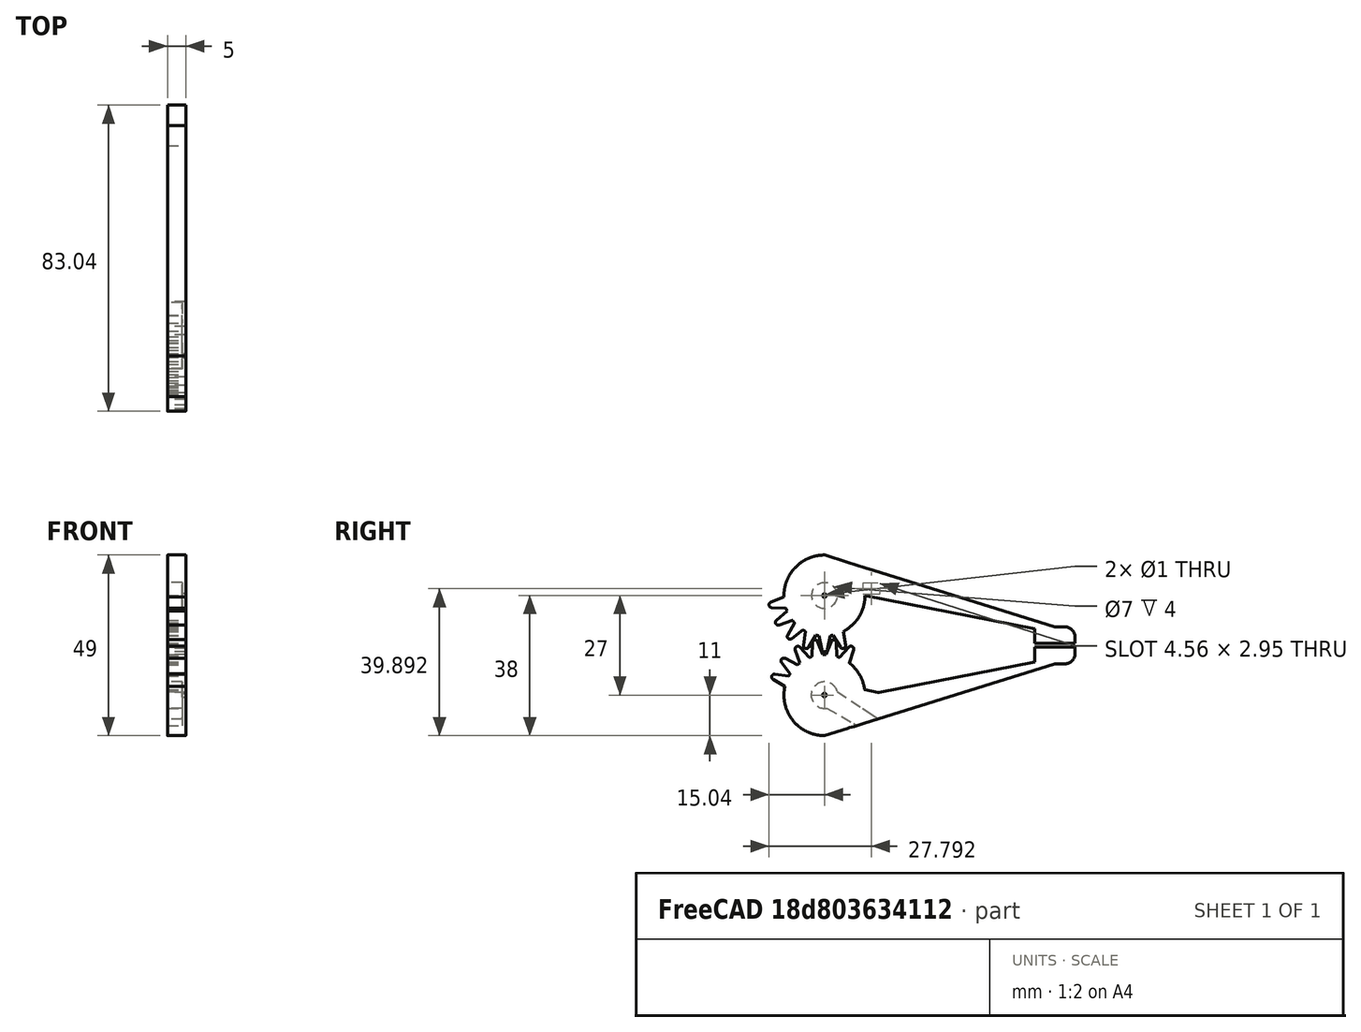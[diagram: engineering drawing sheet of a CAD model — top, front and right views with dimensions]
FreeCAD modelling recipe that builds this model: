
FCSTD DOCUMENT  (FreeCAD 0.20R29177 +426 (Git))
Label: gripper
License: All rights reserved
LicenseURL: http://en.wikipedia.org/wiki/All_rights_reserved
objects: Sketcher::SketchObject×10, PartDesign::Pocket×6, PartDesign::Pad×4, Mesh::Feature×2, PartDesign::PolarPattern×2, PartDesign::Body×2
note: 34 computed .brp shape members not serialized (recipe doc carries the construction recipe); baked Part::Feature solids carry a one-line shape summary decoded from their .brp

FEATURE [Mesh::Feature] ServoGripper90g_v1_A  label="ServoGripper90g_v1-A"
  Placement = pos=(0,0,-27) rot=(0,0,1;0rad)
FEATURE [Sketcher::SketchObject] Sketch  label="larm"
  FullyConstrained = true
  MapMode = 5
  Placement = pos=(0,0,0) rot=(0.57735,0.57735,0.57735;2.0944rad)
  Support = -> [YZ_Plane]
  sketch-geometry (9):
    g0: ArcOfCircle CenterX=0 CenterY=0 CenterZ=0 NormalX=0 NormalY=0 NormalZ=1 AngleXU=0 Radius=11 StartAngle=0 EndAngle=5.0362
    g1: LineSegment StartX=57 StartY=13 StartZ=0 EndX=68 EndY=13 EndZ=0
    g2: LineSegment StartX=68 StartY=13 StartZ=0 EndX=68 EndY=11.2 EndZ=0
    g3: LineSegment StartX=65.3 StartY=8.5 StartZ=0 EndX=62.5 EndY=8.5 EndZ=0
    g4: LineSegment StartX=57 StartY=9 StartZ=0 EndX=57 EndY=13 EndZ=0
    g5: GeomPoint X=62.5 Y=8.5 Z=0
    g6: LineSegment StartX=11 StartY=0 StartZ=0 EndX=57 EndY=9 EndZ=0
    g7: LineSegment StartX=62.5 StartY=8.5 StartZ=0 EndX=3.5 EndY=-10.4283 EndZ=0
    g8: ArcOfCircle CenterX=65.3 CenterY=11.2 CenterZ=0 NormalX=0 NormalY=0 NormalZ=1 AngleXU=0 Radius=2.7 StartAngle=4.71239 EndAngle=6.28319
  constraints (25):
    c: Coincident(g0,g-1)
    c: Radius(g0) = 11
    c: Coincident(g1,g2)
    c: Coincident(g4,g1)
    c: Horizontal(g1)
    c: Horizontal(g3)
    c: Vertical(g2)
    c: Vertical(g4)
    c: DistanceX(g1,g1) = 11
    c: DistanceY(g4,g4) = 4
    c: PointOnObject(g5,g3)
    c: DistanceX(g4,g5) = 5.5
    c: Coincident(g6,g4)
    c: Coincident(g7,g5)
    c: Coincident(g0,g7)
    c: PointOnObject(g3,g7)
    c: Tangent(g2,g8) = 1.5708
    c: Tangent(g3,g8) = 1.5708
    c: DistanceY(g0,g1) = 13
    c: DistanceX(g0,g3) = 62.5
    c: DistanceY(g0,g3) = 8.5
    c: Coincident(g0,g6)
    c: DistanceY(g0,g0) = 0
    c: DistanceX(g3,g3) = 2.8
    c: DistanceX(g0,g0) = 3.5
FEATURE [PartDesign::Pad] Pad  label="pad_larm"
  Direction = (1,-2e-16,3e-16)
  Length = 5
  Length2 = 10
  Placement = pos=(0,0,0) rot=(0.57735,0.57735,0.57735;2.0944rad)
  Profile = -> Sketch
  ReferenceAxis = -> Sketch [N_Axis]
  Type = 0
FEATURE [Sketcher::SketchObject] Sketch001  label="lgear"
  FullyConstrained = true
  MapMode = 5
  Placement = pos=(0,0,0) rot=(0.57735,0.57735,0.57735;2.0944rad)
  Support = -> [YZ_Plane]
  sketch-geometry (4):
    g0: ArcOfCircle CenterX=0 CenterY=0 CenterZ=0 NormalX=0 NormalY=0 NormalZ=1 AngleXU=0 Radius=11 StartAngle=0.911421 EndAngle=1.185
    g1: LineSegment StartX=4.13926 StartY=10.1915 StartZ=0 EndX=6.62638 EndY=13.0068 EndZ=0
    g2: LineSegment StartX=7.92617 StartY=12.2581 StartZ=0 EndX=6.73886 EndY=8.69413 EndZ=0
    g3: ArcOfCircle CenterX=7.2 CenterY=12.5 CenterZ=0 NormalX=0 NormalY=0 NormalZ=1 AngleXU=0 Radius=0.76541 StartAngle=5.9616 EndAngle=8.70119
  constraints (11):
    c: Coincident(g0,g-1)
    c: Radius(g0) = 11
    c: Distance(g0,g0) = 3
    c: Coincident(g1,g0)
    c: Coincident(g2,g0)
    c: Equal(g2,g1)
    c: Tangent(g1,g3) = 1.5708
    c: Tangent(g2,g3) = 1.5708
    c: DistanceX(g0,g3) = 7.2
    c: DistanceY(g0,g3) = 12.5
    c: Distance(g1,g2) = 1.5
FEATURE [PartDesign::Pad] Pad001  label="pad_lgear"
  BaseFeature = -> Pad
  Direction = (1,-2e-16,3e-16)
  Length = 5
  Length2 = 10
  Placement = pos=(0,0,0) rot=(0.57735,0.57735,0.57735;2.0944rad)
  Profile = -> Sketch001
  ReferenceAxis = -> Sketch001 [N_Axis]
  Type = 0
FEATURE [PartDesign::PolarPattern] PolarPattern  label="gear_teeth"
  Angle = 360
  Axis = -> Sketch001 [N_Axis]
  BaseFeature = -> Pad001
  Occurrences = 18
  Originals = -> [Pad001]
  Placement = pos=(0,0,0) rot=(0.57735,0.57735,0.57735;2.0944rad)
FEATURE [Sketcher::SketchObject] Sketch002  label="main_cleaner"
  ExternalGeometry = -> [PolarPattern]
  FullyConstrained = true
  MapMode = 5
  Placement = pos=(0,0,0) rot=(0.57735,0.57735,0.57735;2.0944rad)
  Support = -> [YZ_Plane]
  sketch-geometry (9):
    g0: ArcOfCircle CenterX=0 CenterY=0 CenterZ=0 NormalX=0 NormalY=0 NormalZ=1 AngleXU=0 Radius=11 StartAngle=2.95876 EndAngle=4.71239
    g1: ArcOfCircle CenterX=0 CenterY=0 CenterZ=0 NormalX=0 NormalY=0 NormalZ=1 AngleXU=0 Radius=11 StartAngle=0.182835 EndAngle=0.875996
    g2: LineSegment StartX=10.8167 StartY=2 StartZ=0 EndX=17.8885 EndY=2 EndZ=0
    g3: LineSegment StartX=-2e-15 StartY=-11 StartZ=0 EndX=62.5 EndY=8.5 EndZ=0
    g4: LineSegment StartX=62.5 StartY=8.5 StartZ=0 EndX=0 EndY=-18 EndZ=0
    g5: ArcOfCircle CenterX=0 CenterY=0 CenterZ=0 NormalX=0 NormalY=0 NormalZ=1 AngleXU=0 Radius=16 StartAngle=0.963507 EndAngle=2.84983
    g6: LineSegment StartX=-10.8167 StartY=2 StartZ=0 EndX=-15.3238 EndY=4.60222 EndZ=0
    g7: LineSegment StartX=7.04255 StartY=8.45 StartZ=0 EndX=9.1303 EndY=13.1392 EndZ=0
    g8: ArcOfCircle CenterX=0 CenterY=0 CenterZ=0 NormalX=0 NormalY=0 NormalZ=1 AngleXU=0 Radius=18 StartAngle=0.111341 EndAngle=4.71239
  constraints (26):
    c: Coincident(g0,g-1)
    c: PointOnObject(g0,g-2)
    c: PointOnObject(g4,g-2)
    c: Coincident(g1,g0)
    c: Coincident(g2,g1)
    c: Radius(g1) = 11
    c: Coincident(g3,g0)
    c: Coincident(g3,g-3)
    c: Coincident(g4,g3)
    c: Radius(g0) = 11
    c: Coincident(g7,g1)
    c: Coincident(g7,g5)
    c: Coincident(g6,g5)
    c: Coincident(g0,g6)
    c: Coincident(g8,g0)
    c: Coincident(g8,g4)
    c: Coincident(g8,g2)
    c: Radius(g8) = 18
    c: Coincident(g5,g0)
    c: Horizontal(g2)
    c: Angle(g7) = 1.15192
    c: Angle(g6) = 2.61799
    c: DistanceY(g1,g0) = 0
    c: DistanceY(g0,g0) = 2
    c: Radius(g5) = 16
    c: DistanceY(g0,g1) = 8.45
FEATURE [Sketcher::SketchObject] Sketch003  label="servo_mover"
  FullyConstrained = true
  MapMode = 5
  Placement = pos=(0,0,0) rot=(0.57735,0.57735,0.57735;2.0944rad)
  Support = -> [YZ_Plane]
  sketch-geometry (4):
    g0: ArcOfCircle CenterX=0 CenterY=0 CenterZ=0 NormalX=0 NormalY=0 NormalZ=1 AngleXU=0 Radius=3.6 StartAngle=0.289687 EndAngle=4.88265
    g1: LineSegment StartX=0.61 StartY=-3.54794 StartZ=0 EndX=11.61 EndY=-9.81644 EndZ=0
    g2: LineSegment StartX=3.45 StartY=1.02835 StartZ=0 EndX=13.95 EndY=-6.04584 EndZ=0
    g3: ArcOfCircle CenterX=12.7094 CenterY=-7.88729 CenterZ=0 NormalX=0 NormalY=0 NormalZ=1 AngleXU=0 Radius=2.2204 StartAngle=4.19442 EndAngle=7.2611
  constraints (11):
    c: Coincident(g0,g-1)
    c: Radius(g0) = 3.6
    c: Equal(g2,g1)
    c: Tangent(g1,g3) = -1.5708
    c: Tangent(g2,g3) = 1.5708
    c: Coincident(g0,g1)
    c: Coincident(g0,g2)
    c: DistanceX(g0,g0) = 3.45
    c: DistanceX(g0,g1) = 11.61
    c: DistanceX(g0,g2) = 13.95
    c: DistanceX(g0,g0) = 0.61
FEATURE [PartDesign::Pocket] Pocket001  label="servo_mover_pocket"
  BaseFeature = -> PolarPattern
  Direction = (-1,2e-16,-3e-16)
  Length = 4
  Length2 = 5
  Placement = pos=(0,0,0) rot=(0.57735,0.57735,0.57735;2.0944rad)
  Profile = -> Sketch003
  ReferenceAxis = -> Sketch003 [N_Axis]
  Reversed = true
  Type = 0
FEATURE [Sketcher::SketchObject] Sketch004  label="servo_screw"
  FullyConstrained = true
  MapMode = 5
  Placement = pos=(0,0,0) rot=(0.57735,0.57735,0.57735;2.0944rad)
  Support = -> [YZ_Plane]
  sketch-geometry (1):
    g0: Circle CenterX=0 CenterY=0 CenterZ=0 NormalX=0 NormalY=0 NormalZ=1 AngleXU=0 Radius=0.5
  constraints (2):
    c: Coincident(g0,g-1)
    c: Radius(g0) = 0.5
FEATURE [PartDesign::Pocket] Pocket002  label="screw"
  BaseFeature = -> Pocket001
  Direction = (-1,2e-16,-3e-16)
  Length = 5
  Length2 = 5
  Midplane = true
  Placement = pos=(0,0,0) rot=(0.57735,0.57735,0.57735;2.0944rad)
  Profile = -> Sketch004
  ReferenceAxis = -> Sketch004 [N_Axis]
  Type = 1
FEATURE [Sketcher::SketchObject] Sketch005  label="rarm"
  FullyConstrained = true
  MapMode = 5
  Placement = pos=(0,0,0) rot=(0.57735,0.57735,0.57735;2.0944rad)
  Support = -> [YZ_Plane001]
  sketch-geometry (9):
    g0: ArcOfCircle CenterX=0 CenterY=0 CenterZ=0 NormalX=0 NormalY=0 NormalZ=1 AngleXU=0 Radius=11 StartAngle=1.5708 EndAngle=6.28319
    g1: LineSegment StartX=62.5 StartY=-8.5 StartZ=0 EndX=65.3 EndY=-8.5 EndZ=0
    g2: LineSegment StartX=68 StartY=-11.2 StartZ=0 EndX=68 EndY=-13 EndZ=0
    g3: LineSegment StartX=68 StartY=-13 StartZ=0 EndX=57 EndY=-13 EndZ=0
    g4: LineSegment StartX=57 StartY=-13 StartZ=0 EndX=57 EndY=-9 EndZ=0
    g5: LineSegment StartX=11 StartY=-2.7e-15 StartZ=0 EndX=57 EndY=-9 EndZ=0
    g6: GeomPoint X=62.5 Y=-8.5 Z=0
    g7: LineSegment StartX=7e-16 StartY=11 StartZ=0 EndX=62.5 EndY=-8.5 EndZ=0
    g8: ArcOfCircle CenterX=65.3 CenterY=-11.2 CenterZ=0 NormalX=0 NormalY=0 NormalZ=1 AngleXU=0 Radius=2.7 StartAngle=0 EndAngle=1.5708
  constraints (25):
    c: Coincident(g0,g-1)
    c: Radius(g0) = 11
    c: Coincident(g2,g3)
    c: Coincident(g3,g4)
    c: Horizontal(g1)
    c: Horizontal(g3)
    c: Vertical(g2)
    c: Vertical(g4)
    c: DistanceX(g3,g3) = 11
    c: Coincident(g5,g4)
    c: DistanceY(g4,g4) = 4
    c: PointOnObject(g6,g1)
    c: Coincident(g7,g6)
    c: DistanceY(g2,g0) = 13
    c: DistanceX(g0,g7) = 62.5
    c: DistanceX(g7,g-1) = 0
    c: Coincident(g0,g5)
    c: Coincident(g0,g7)
    c: DistanceY(g0,g0) = 0
    c: PointOnObject(g1,g7)
    c: DistanceY(g1,g0) = 8.5
    c: Tangent(g1,g8) = 1.5708
    c: Tangent(g2,g8) = 1.5708
    c: DistanceX(g1,g1) = 2.8
    c: DistanceX(g0,g2) = 68
FEATURE [PartDesign::Pad] Pad002  label="rarm_pad"
  Direction = (1,-2e-16,3e-16)
  Length = 5
  Length2 = 10
  Placement = pos=(0,0,0) rot=(0.57735,0.57735,0.57735;2.0944rad)
  Profile = -> Sketch005
  ReferenceAxis = -> Sketch005 [N_Axis]
  Type = 0
FEATURE [PartDesign::Pocket] Pocket
  BaseFeature = -> Pocket002
  Direction = (-1,2e-16,-3e-16)
  Length = 5
  Length2 = 5
  Placement = pos=(0,0,0) rot=(0.57735,0.57735,0.57735;2.0944rad)
  Profile = -> Sketch002
  ReferenceAxis = -> Sketch002 [N_Axis]
  Reversed = true
  Type = 1
FEATURE [PartDesign::Body] Body  label="left_side"
  Group = -> [Sketch,Pad,Sketch001,Pad001,PolarPattern,Sketch002,Sketch003,Pocket001,Sketch004,Pocket002,Pocket]
  Origin = -> Origin
  Placement = pos=(0,0,-27) rot=(0,0,1;0rad)
  Tip = -> Pocket
FEATURE [Sketcher::SketchObject] Sketch006  label="r_gear"
  FullyConstrained = true
  MapMode = 5
  Placement = pos=(0,0,0) rot=(0.57735,0.57735,0.57735;2.0944rad)
  Support = -> [YZ_Plane001]
  sketch-geometry (4):
    g0: ArcOfCircle CenterX=0 CenterY=0 CenterZ=0 NormalX=0 NormalY=0 NormalZ=1 AngleXU=0 Radius=11 StartAngle=4.5756 EndAngle=4.84918
    g1: LineSegment StartX=-1.5 StartY=-10.8972 StartZ=0 EndX=-0.75 EndY=-14.6499 EndZ=0
    g2: LineSegment StartX=0.75 StartY=-14.6499 StartZ=0 EndX=1.5 EndY=-10.8972 EndZ=0
    g3: ArcOfCircle CenterX=0 CenterY=-14.5 CenterZ=0 NormalX=0 NormalY=0 NormalZ=1 AngleXU=0 Radius=0.764832 StartAngle=3.33885 EndAngle=6.08593
  constraints (11):
    c: Coincident(g0,g-1)
    c: Radius(g0) = 11
    c: Coincident(g1,g0)
    c: Coincident(g2,g0)
    c: Equal(g1,g2)
    c: DistanceX(g0,g0) = 3
    c: Tangent(g1,g3) = -1.5708
    c: Tangent(g2,g3) = -1.5708
    c: PointOnObject(g3,g-2)
    c: DistanceX(g1,g2) = 1.5
    c: DistanceY(g3,g0) = 14.5
FEATURE [PartDesign::Pad] Pad003  label="r_gear_pad"
  BaseFeature = -> Pad002
  Direction = (1,-2e-16,3e-16)
  Length = 5
  Length2 = 10
  Placement = pos=(0,0,0) rot=(0.57735,0.57735,0.57735;2.0944rad)
  Profile = -> Sketch006
  ReferenceAxis = -> Sketch006 [N_Axis]
  Type = 0
FEATURE [PartDesign::PolarPattern] PolarPattern001  label="r_gear_teeth"
  Angle = 360
  Axis = -> Sketch006 [N_Axis]
  BaseFeature = -> Pad003
  Occurrences = 18
  Originals = -> [Pad003]
  Placement = pos=(0,0,0) rot=(0.57735,0.57735,0.57735;2.0944rad)
FEATURE [Sketcher::SketchObject] Sketch007  label="rcleaner"
  ExternalGeometry = -> [PolarPattern001]
  FullyConstrained = true
  MapMode = 5
  Placement = pos=(0,0,0) rot=(0.57735,0.57735,0.57735;2.0944rad)
  Support = -> [YZ_Plane001]
  sketch-geometry (9):
    g0: ArcOfCircle CenterX=0 CenterY=0 CenterZ=0 NormalX=0 NormalY=0 NormalZ=1 AngleXU=0 Radius=11 StartAngle=1.5708 EndAngle=3.14159
    g1: LineSegment StartX=7e-16 StartY=11 StartZ=0 EndX=62.5 EndY=-8.5 EndZ=0
    g2: LineSegment StartX=1.1e-15 StartY=18 StartZ=0 EndX=62.5 EndY=-8.5 EndZ=0
    g3: LineSegment StartX=11 StartY=-1.25e-14 StartZ=0 EndX=17.8571 EndY=-2.26378 EndZ=0
    g4: ArcOfCircle CenterX=0 CenterY=0 CenterZ=0 NormalX=0 NormalY=0 NormalZ=1 AngleXU=0 Radius=11 StartAngle=5.24019 EndAngle=6.28319
    g5: ArcOfCircle CenterX=0 CenterY=0 CenterZ=0 NormalX=0 NormalY=0 NormalZ=1 AngleXU=0 Radius=16 StartAngle=3.27616 EndAngle=5.22944
    g6: LineSegment StartX=-11 StartY=1.3e-15 StartZ=0 EndX=-15.8554 EndY=-2.14653 EndZ=0
    g7: LineSegment StartX=5.54 StartY=-9.50307 StartZ=0 EndX=7.9091 EndY=-13.9085 EndZ=0
    g8: ArcOfCircle CenterX=0 CenterY=0 CenterZ=0 NormalX=0 NormalY=0 NormalZ=1 AngleXU=0 Radius=18 StartAngle=1.5708 EndAngle=6.15709
  constraints (25):
    c: Coincident(g0,g-1)
    c: Radius(g0) = 11
    c: PointOnObject(g0,g-2)
    c: Coincident(g1,g0)
    c: Coincident(g1,g-3)
    c: PointOnObject(g2,g-2)
    c: Coincident(g2,g1)
    c: Coincident(g3,g-4)
    c: Coincident(g4,g0)
    c: Coincident(g4,g3)
    c: Coincident(g5,g0)
    c: Radius(g5) = 16
    c: Coincident(g6,g0)
    c: Coincident(g6,g5)
    c: Coincident(g7,g4)
    c: Coincident(g7,g5)
    c: Coincident(g8,g0)
    c: Coincident(g8,g2)
    c: Coincident(g8,g3)
    c: Radius(g8) = 18
    c: Angle(g6) = -2.72533
    c: Angle(g3) = -0.318872
    c: Angle(g7) = -1.07739
    c: DistanceX(g0,g4) = 5.54
    c: DistanceY(g0,g0) = 0
FEATURE [PartDesign::Pocket] Pocket003  label="rclean"
  BaseFeature = -> PolarPattern001
  Direction = (-1,2e-16,-3e-16)
  Length = 5
  Length2 = 5
  Placement = pos=(0,0,0) rot=(0.57735,0.57735,0.57735;2.0944rad)
  Profile = -> Sketch007
  ReferenceAxis = -> Sketch007 [N_Axis]
  Reversed = true
  Type = 1
FEATURE [Sketcher::SketchObject] Sketch008
  FullyConstrained = true
  MapMode = 5
  Placement = pos=(0,0,0) rot=(0.57735,0.57735,0.57735;2.0944rad)
  Support = -> [YZ_Plane001]
  sketch-geometry (1):
    g0: Circle CenterX=0 CenterY=0 CenterZ=0 NormalX=0 NormalY=0 NormalZ=1 AngleXU=0 Radius=3.5
  constraints (2):
    c: Coincident(g0,g-1)
    c: Radius(g0) = 3.5
FEATURE [PartDesign::Pocket] Pocket004
  BaseFeature = -> Pocket003
  Direction = (-1,2e-16,-3e-16)
  Length = 4
  Length2 = 5
  Placement = pos=(0,0,0) rot=(0.57735,0.57735,0.57735;2.0944rad)
  Profile = -> Sketch008
  ReferenceAxis = -> Sketch008 [N_Axis]
  Reversed = true
  Type = 0
FEATURE [Sketcher::SketchObject] Sketch009
  FullyConstrained = true
  MapMode = 5
  Placement = pos=(0,0,0) rot=(0.57735,0.57735,0.57735;2.0944rad)
  Support = -> [YZ_Plane001]
  sketch-geometry (1):
    g0: Circle CenterX=0 CenterY=0 CenterZ=0 NormalX=0 NormalY=0 NormalZ=1 AngleXU=0 Radius=0.5
  constraints (2):
    c: Coincident(g0,g-1)
    c: Radius(g0) = 0.5
FEATURE [PartDesign::Pocket] Pocket005
  BaseFeature = -> Pocket004
  Direction = (-1,2e-16,-3e-16)
  Length = 5
  Length2 = 5
  Placement = pos=(0,0,0) rot=(0.57735,0.57735,0.57735;2.0944rad)
  Profile = -> Sketch009
  ReferenceAxis = -> Sketch009 [N_Axis]
  Reversed = true
  Type = 1
FEATURE [PartDesign::Body] Body001  label="right_side"
  Group = -> [Sketch005,Pad002,Sketch006,Pad003,PolarPattern001,Sketch007,Pocket003,Sketch008,Pocket004,Sketch009,Pocket005]
  Origin = -> Origin001
  Tip = -> Pocket005
FEATURE [Mesh::Feature] gripper_SCALE
